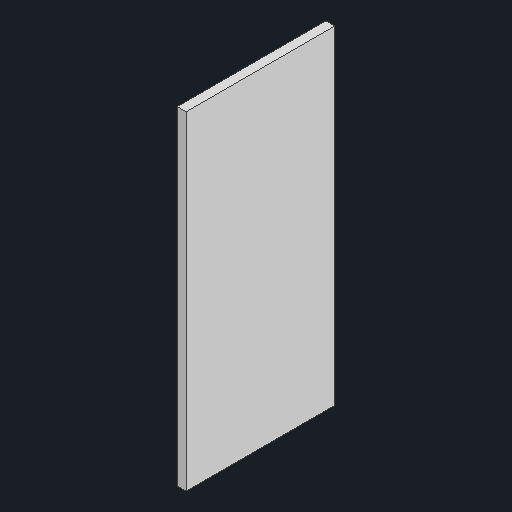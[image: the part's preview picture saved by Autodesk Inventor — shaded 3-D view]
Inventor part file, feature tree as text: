
AUTODESK INVENTOR PART (.ipt)
format: ipt  version: 2022 (Build 260153000, 153)  size: 221,184 bytes
history: native  units: in
note: dims shown in document units (in); Inventor stores cm internally (conversion verified against a paired STEP export)
features: other x3, extrude x1, sketch x1, reference x1
ambient origin geometry x8: Origin, YZ Plane, XZ Plane, XY Plane, X Axis, Y Axis, Z Axis, Center Point
bodies: Solid1 (feature_tree)
feature tree (6):
  extrude  "Extrusion1"  Depth=1.0in TaperAngle=0.0deg
  sketch  "Sketch1"  dims[d0=0.02in d1=1.0in d2=0.0in]
  reference  "Reference1"
  parser-record x1  (decoder bookkeeping rows leaked as tree rows — omitted from the tree; the rows remain in map.json)
  other  "Prototype Assembly.iam"
  other  "Base:1"
note: 1 file-system path scrubbed to <path> (originals preserved in map.json)
